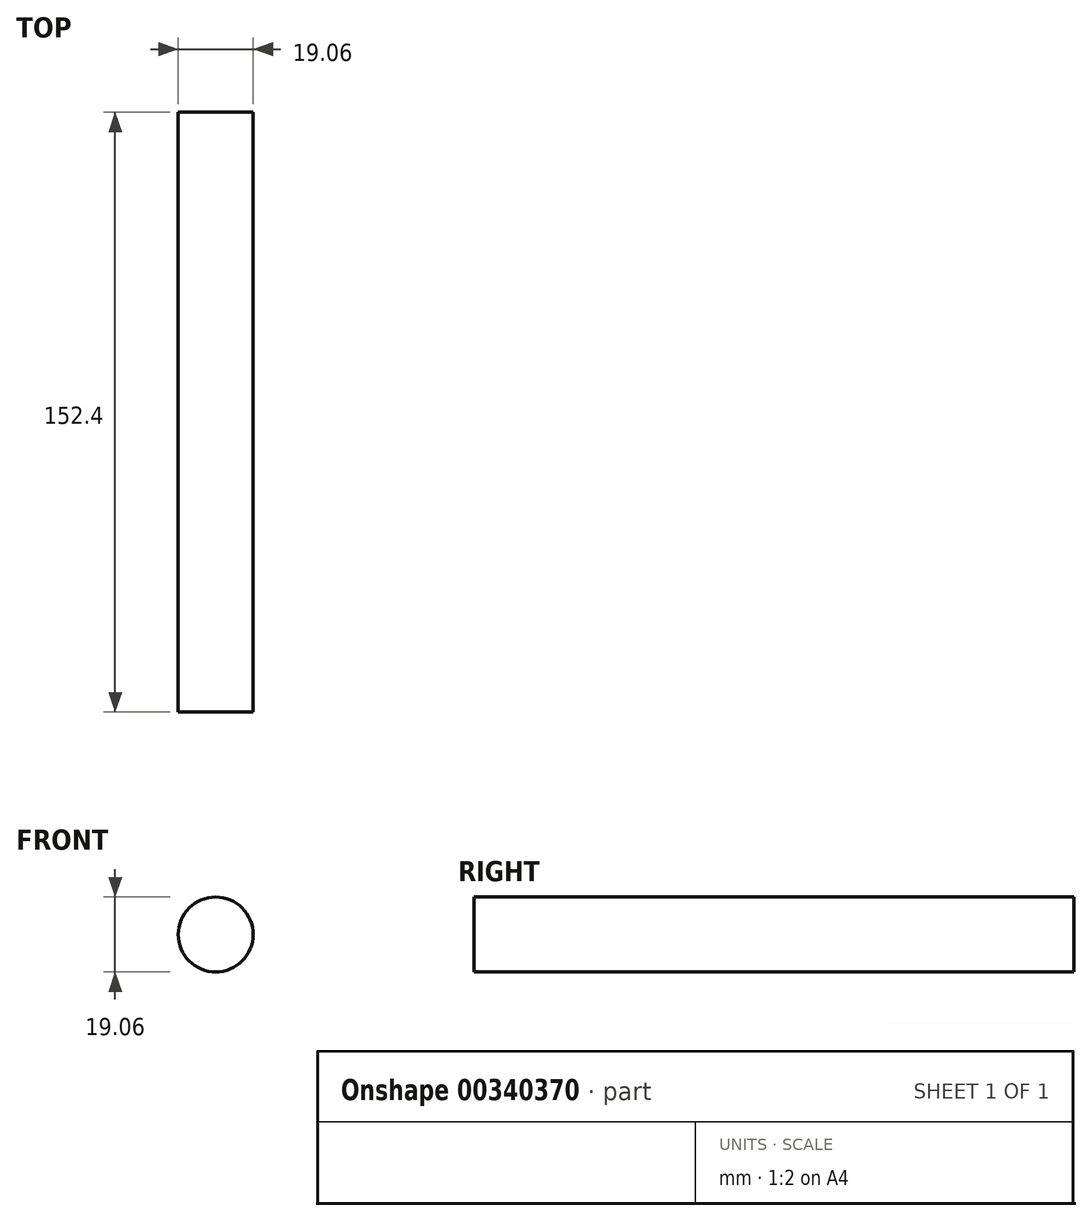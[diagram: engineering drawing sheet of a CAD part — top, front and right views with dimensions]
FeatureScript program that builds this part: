
annotation { "Feature Type Name" : "Feature", "Feature Type Description" : "" }
export const myFeature = defineFeature(function(context is Context, id is Id, definition is map)
    precondition{}
    {
        {
            var Q0;
            Q0=qCreatedBy(makeId("Front.planeOp"),FACE);
            var sketch = newSketch(context, id + "F0", { "sketchPlane" : qUnion([Q0])});
            skCircle(sketch, "E0", {"center": v(0, 0) * mm, "radius": 9.53 * mm});
            skSolve(sketch);
        }
        {
            var Q0;
            Q0=makeQuery(id+"F0.imprint","IMPRINT",FACE,{"disambiguationData":[TD([[makeQuery(id+"F0.imprint","IMPRINT",EDGE,{"derivedFrom":sQuery(id+"F0.wireOp",EDGE,"E0")}),1.0]])]});
            extrude(context, id + "F1", {"entities" : qUnion([Q0]), "depth" : 152.4 * mm});
        }
    });
